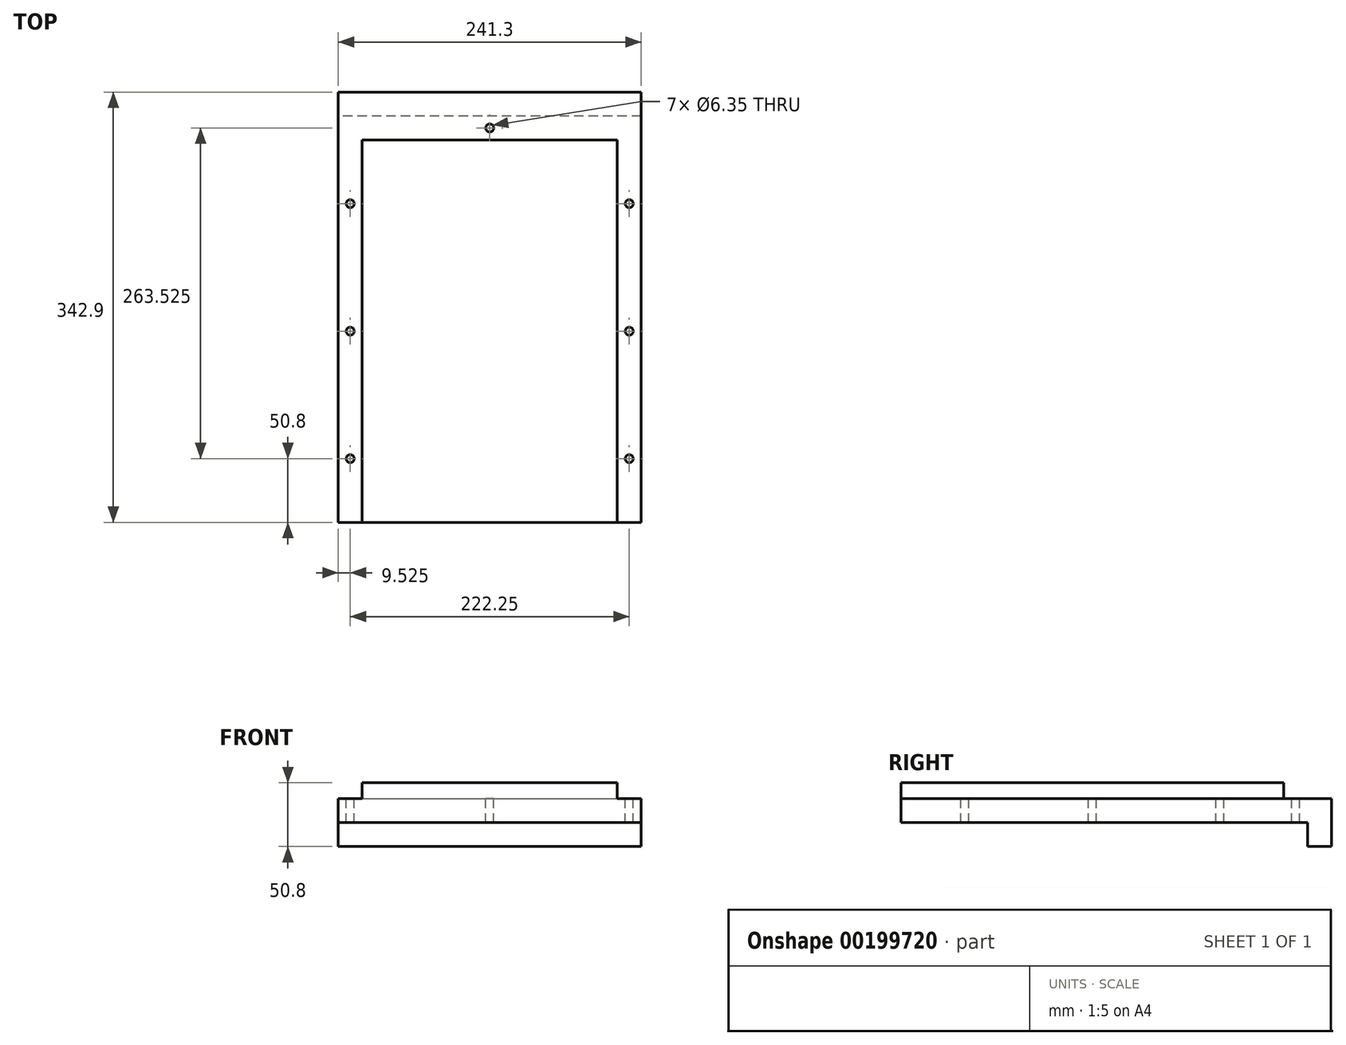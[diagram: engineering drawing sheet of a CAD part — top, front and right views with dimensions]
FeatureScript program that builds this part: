
annotation { "Feature Type Name" : "Feature", "Feature Type Description" : "" }
export const myFeature = defineFeature(function(context is Context, id is Id, definition is map)
    precondition{}
    {
        {
            var Q0;
            Q0=qCreatedBy(makeId("Top.planeOp"),FACE);
            var sketch = newSketch(context, id + "F0", { "sketchPlane" : qUnion([Q0])});
            skLineSegment(sketch, "E0.bottom", {"start": v(-101.6, 152.4) * mm, "end": v(101.6, 152.4) * mm});
            skLineSegment(sketch, "E0.top", {"start": v(-101.6, -152.4) * mm, "end": v(101.6, -152.4) * mm});
            skLineSegment(sketch, "E0.left", {"start": v(-101.6, 152.4) * mm, "end": v(-101.6, -152.4) * mm});
            skLineSegment(sketch, "E0.right", {"start": v(101.6, 152.4) * mm, "end": v(101.6, -152.4) * mm});
            skLineSegment(sketch, "E1", {"start": v(-101.6, 152.4) * mm, "end": v(101.6, -152.4) * mm, "construction": true});
            skSolve(sketch);
        }
        {
            var Q0;
            Q0 = qSketchRegion(id + "F0", true);
            extrude(context, id + "F1", {"entities" : qUnion([Q0]), "depth" : 12.7 * mm, "offsetDistance" : 25.4 * mm});
        }
        {
            var Q0;
            Q0=makeQuery(id+"F1.opExtrude","CAP_FACE",FACE,{"disambiguationData":[OSD([sQuery(id+"F0.wireOp",EDGE,"E0.bottom"),sQuery(id+"F0.wireOp",EDGE,"E0.top"),sQuery(id+"F0.wireOp",EDGE,"E0.left"),sQuery(id+"F0.wireOp",EDGE,"E0.right")])],"isStart":true});
            var sketch = newSketch(context, id + "F2", { "sketchPlane" : qUnion([Q0])});
            skLineSegment(sketch, "E2.bottom", {"start": v(-120.65, 152.4) * mm, "end": v(120.65, 152.4) * mm});
            skLineSegment(sketch, "E2.top", {"start": v(-120.65, -190.5) * mm, "end": v(120.65, -190.5) * mm});
            skLineSegment(sketch, "E2.left", {"start": v(-120.65, 152.4) * mm, "end": v(-120.65, -190.5) * mm});
            skLineSegment(sketch, "E2.right", {"start": v(120.65, 152.4) * mm, "end": v(120.65, -190.5) * mm});
            skSolve(sketch);
        }
        {
            var Q0;
            Q0 = qSketchRegion(id + "F2", true);
            extrude(context, id + "F3", {"entities" : qUnion([Q0]), "operationType" : NewBodyOperationType.ADD, "depth" : 19.05 * mm, "offsetDistance" : 25.4 * mm});
        }
        {
            var Q0;
            Q0=makeQuery(id+"F3.opExtrude","CAP_FACE",FACE,{"disambiguationData":[OSD([sQuery(id+"F2.wireOp",EDGE,"E2.bottom"),sQuery(id+"F2.wireOp",EDGE,"E2.top"),sQuery(id+"F2.wireOp",EDGE,"E2.left"),sQuery(id+"F2.wireOp",EDGE,"E2.right")])],"isStart":false});
            var sketch = newSketch(context, id + "F4", { "sketchPlane" : qUnion([Q0])});
            skLineSegment(sketch, "E3.bottom", {"start": v(120.65, -190.5) * mm, "end": v(-120.65, -190.5) * mm});
            skLineSegment(sketch, "E3.top", {"start": v(120.65, -171.45) * mm, "end": v(-120.65, -171.45) * mm});
            skLineSegment(sketch, "E3.left", {"start": v(120.65, -190.5) * mm, "end": v(120.65, -171.45) * mm});
            skLineSegment(sketch, "E3.right", {"start": v(-120.65, -190.5) * mm, "end": v(-120.65, -171.45) * mm});
            skSolve(sketch);
        }
        {
            var Q0;
            Q0 = qSketchRegion(id + "F4", true);
            extrude(context, id + "F5", {"entities" : qUnion([Q0]), "operationType" : NewBodyOperationType.ADD, "depth" : 19.05 * mm, "offsetDistance" : 25.4 * mm});
        }
        {
            var Q0;
            Q0=makeQuery(id+"F3.opExtrude","CAP_FACE",FACE,{"disambiguationData":[OSD([sQuery(id+"F2.wireOp",EDGE,"E2.bottom"),sQuery(id+"F2.wireOp",EDGE,"E2.top"),sQuery(id+"F2.wireOp",EDGE,"E2.left"),sQuery(id+"F2.wireOp",EDGE,"E2.right")])],"isStart":true});
            var sketch = newSketch(context, id + "F6", { "sketchPlane" : qUnion([Q0])});
            skLineSegment(sketch, "E4", {"start": v(-120.65, 161.93) * mm, "end": v(120.65, 161.92) * mm, "construction": true});
            skCircle(sketch, "E5", {"center": v(0, 161.92) * mm, "radius": 3.18 * mm});
            skLineSegment(sketch, "E6", {"start": v(111.12, 161.92) * mm, "end": v(111.12, -152.4) * mm, "construction": true});
            skCircle(sketch, "E7", {"center": v(111.12, 101.6) * mm, "radius": 3.18 * mm});
            skCircle(sketch, "E8", {"center": v(111.12, -101.6) * mm, "radius": 3.18 * mm});
            skCircle(sketch, "E9", {"center": v(111.12, 0) * mm, "radius": 3.18 * mm});
            skLineSegment(sketch, "E10", {"start": v(0, 0) * mm, "end": v(0, 112.38) * mm, "construction": true});
            skCircle(sketch, "E11.MirrorC", {"center": v(-111.12, 101.6) * mm, "radius": 3.18 * mm});
            skCircle(sketch, "E12.MirrorC", {"center": v(-111.12, 0) * mm, "radius": 3.18 * mm});
            skCircle(sketch, "E13.MirrorC", {"center": v(-111.12, -101.6) * mm, "radius": 3.18 * mm});
            skSolve(sketch);
        }
        {
            var Q0;
            Q0 = qSketchRegion(id + "F6", true);
            extrude(context, id + "F7", {"entities" : qUnion([Q0]), "operationType" : NewBodyOperationType.REMOVE, "oppositeDirection" : true, "depth" : 25.4 * mm, "offsetDistance" : 25.4 * mm});
        }
    });
